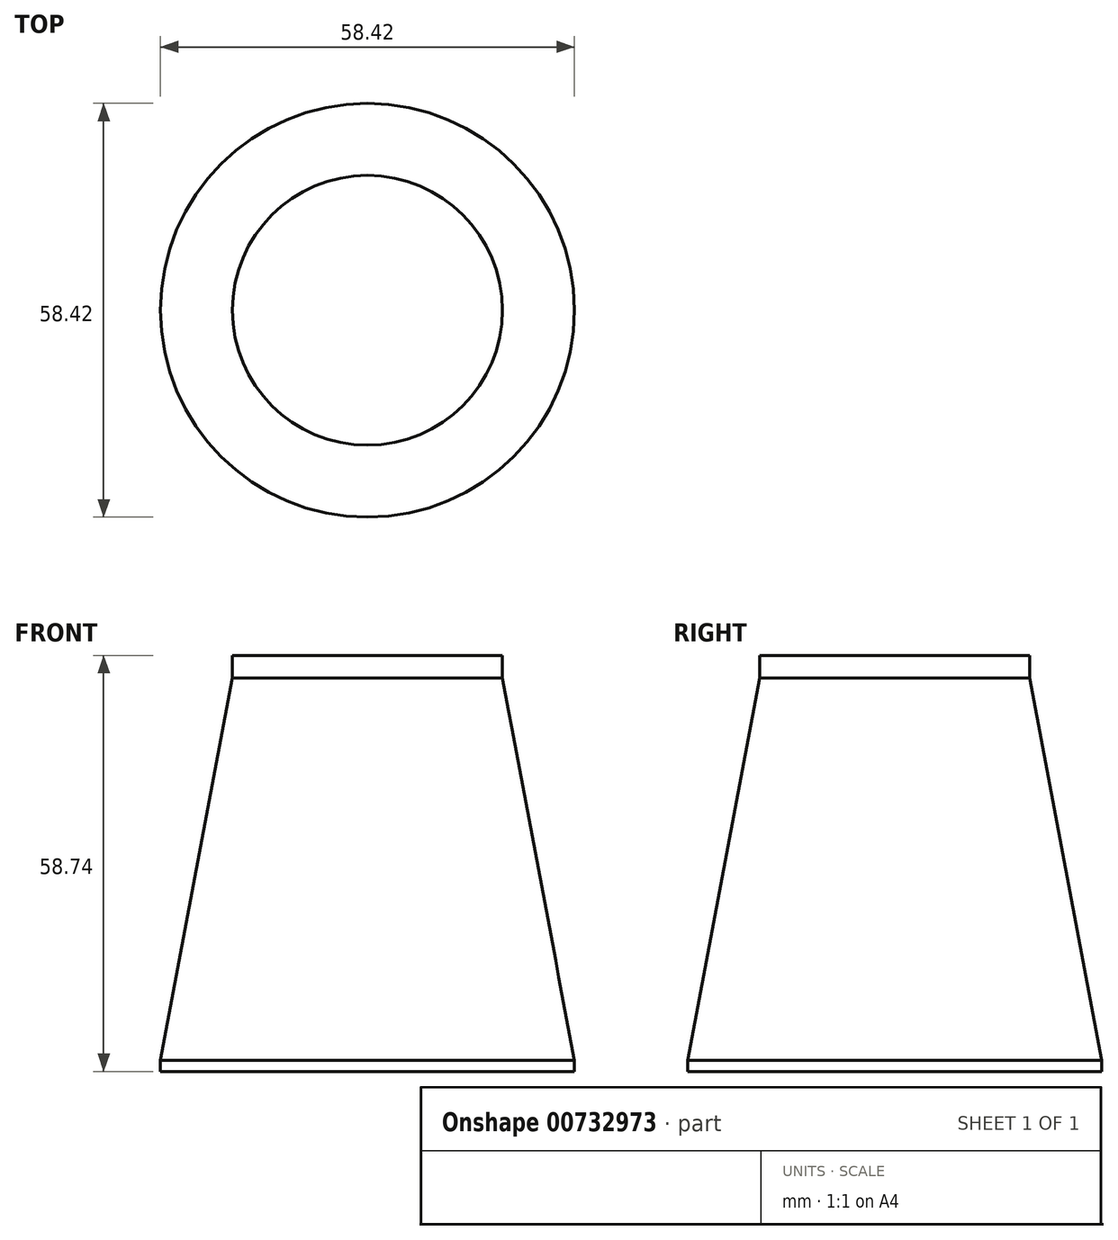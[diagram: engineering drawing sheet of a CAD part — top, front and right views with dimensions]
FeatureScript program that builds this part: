
annotation { "Feature Type Name" : "Feature", "Feature Type Description" : "" }
export const myFeature = defineFeature(function(context is Context, id is Id, definition is map)
    precondition{}
    {
        {
            var Q0;
            Q0=qCreatedBy(makeId("Top.planeOp"),FACE);
            var sketch = newSketch(context, id + "F0", { "sketchPlane" : qUnion([Q0])});
            skCircle(sketch, "E0", {"center": v(0, 0) * mm, "radius": 29.21 * mm});
            skSolve(sketch);
        }
        {
            var Q0;
            Q0=makeQuery(id+"F0.imprint","IMPRINT",FACE,{"disambiguationData":[TD([[makeQuery(id+"F0.imprint","IMPRINT",EDGE,{"derivedFrom":sQuery(id+"F0.wireOp",EDGE,"E0")}),1.0]])]});
            extrude(context, id + "F1", {"entities" : qUnion([Q0]), "depth" : 1.59 * mm, "offsetDistance" : 25.4 * mm});
        }
        {
            var Q0;
            Q0=makeQuery(id+"F1.opExtrude","CAP_FACE",FACE,{"disambiguationData":[OSD([sQuery(id+"F0.wireOp",EDGE,"E0")])],"isStart":false});
            cPlane(context, id + "F2", {"entities" : qUnion([Q0]), "cplaneType" : CPlaneType.OFFSET, "offset" : 53.97 * mm, "width" : 152.4 * mm, "height" : 152.4 * mm});
        }
        {
            var Q0;
            Q0=qCreatedBy(id+"F2.planeOp",FACE);
            var sketch = newSketch(context, id + "F3", { "sketchPlane" : qUnion([Q0])});
            skCircle(sketch, "E1", {"center": v(0, 0) * mm, "radius": 19.05 * mm});
            skSolve(sketch);
        }
        {
            var Q0;
            Q0=makeQuery(id+"F3.imprint","IMPRINT",FACE,{"disambiguationData":[TD([[makeQuery(id+"F3.imprint","IMPRINT",EDGE,{"derivedFrom":sQuery(id+"F3.wireOp",EDGE,"E1")}),1.0]])]});
            extrude(context, id + "F4", {"entities" : qUnion([Q0]), "depth" : 3.17 * mm, "offsetDistance" : 25.4 * mm});
        }
        {
            var Q0;
            Q0=makeQuery(id+"F1.opExtrude","CAP_FACE",FACE,{"disambiguationData":[OSD([sQuery(id+"F0.wireOp",EDGE,"E0")])],"isStart":false});
            var Q1;
            Q1=makeQuery(id+"F4.opExtrude","CAP_FACE",FACE,{"disambiguationData":[OSD([sQuery(id+"F3.wireOp",EDGE,"E1")])],"isStart":true});
            loft(context, id + "F5", {"sheetProfilesArray" : [{ "sheetProfileEntities" : qUnion([Q0]) }, { "sheetProfileEntities" : qUnion([Q1]) }]});
        }
    });
